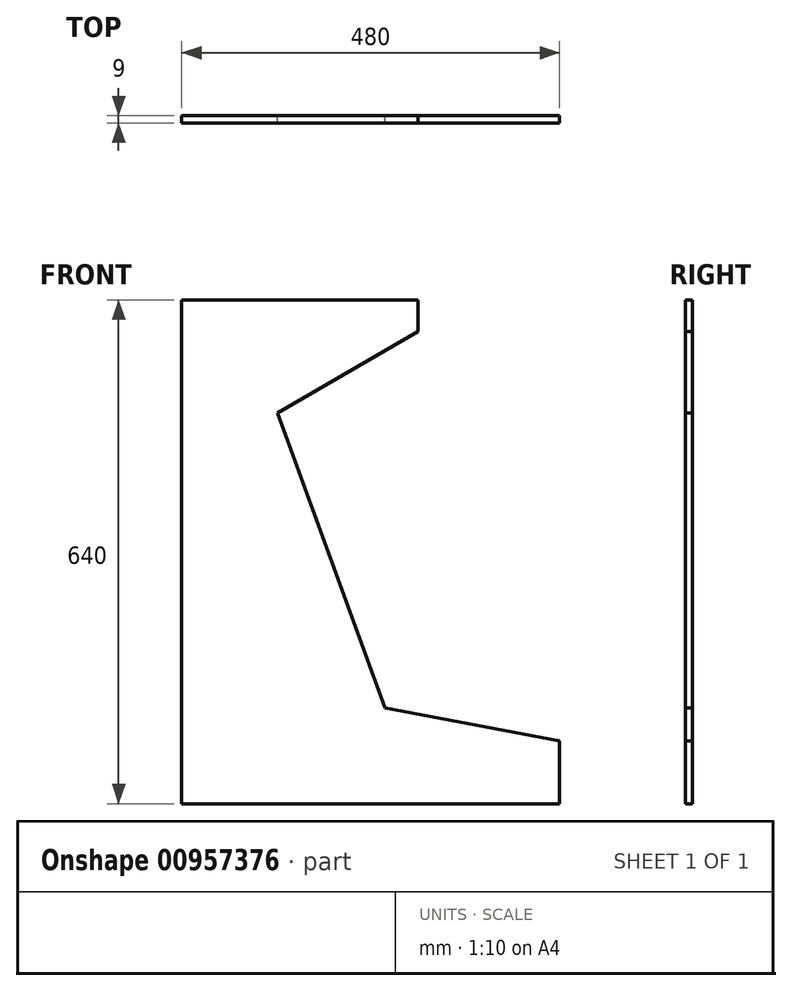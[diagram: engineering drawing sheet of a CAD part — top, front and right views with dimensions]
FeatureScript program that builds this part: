
annotation { "Feature Type Name" : "Feature", "Feature Type Description" : "" }
export const myFeature = defineFeature(function(context is Context, id is Id, definition is map)
    precondition{}
    {
        {
            var Q0;
            Q0=qCreatedBy(makeId("Front.planeOp"),FACE);
            var sketch = newSketch(context, id + "F0", { "sketchPlane" : qUnion([Q0])});
            skLineSegment(sketch, "E0.top", {"start": v(-257.89, -121.73) * mm, "end": v(222.11, -121.73) * mm});
            skLineSegment(sketch, "E0.left", {"start": v(-257.89, 0) * mm, "end": v(-257.89, -121.73) * mm});
            skLineSegment(sketch, "E0.right", {"start": v(222.11, -41.73) * mm, "end": v(222.11, -121.73) * mm});
            skLineSegment(sketch, "E1", {"start": v(0, 0) * mm, "end": v(-136.4, 374.73) * mm});
            skLineSegment(sketch, "E2", {"start": v(-136.4, 374.73) * mm, "end": v(42.11, 478.27) * mm});
            skLineSegment(sketch, "E3", {"start": v(42.11, 478.27) * mm, "end": v(42.11, 518.27) * mm});
            skLineSegment(sketch, "E4", {"start": v(42.11, 518.27) * mm, "end": v(-257.89, 518.27) * mm});
            skLineSegment(sketch, "E5", {"start": v(-257.89, 518.27) * mm, "end": v(-257.89, 0) * mm});
            skLineSegment(sketch, "E6", {"start": v(0, 0) * mm, "end": v(222.11, -41.73) * mm});
            skSolve(sketch);
        }
        {
            var Q0;
            Q0 = qSketchRegion(id + "F0", true);
            extrude(context, id + "F1", {"entities" : qUnion([Q0]), "depth" : 9 * mm, "offsetDistance" : 25 * mm});
        }
    });
